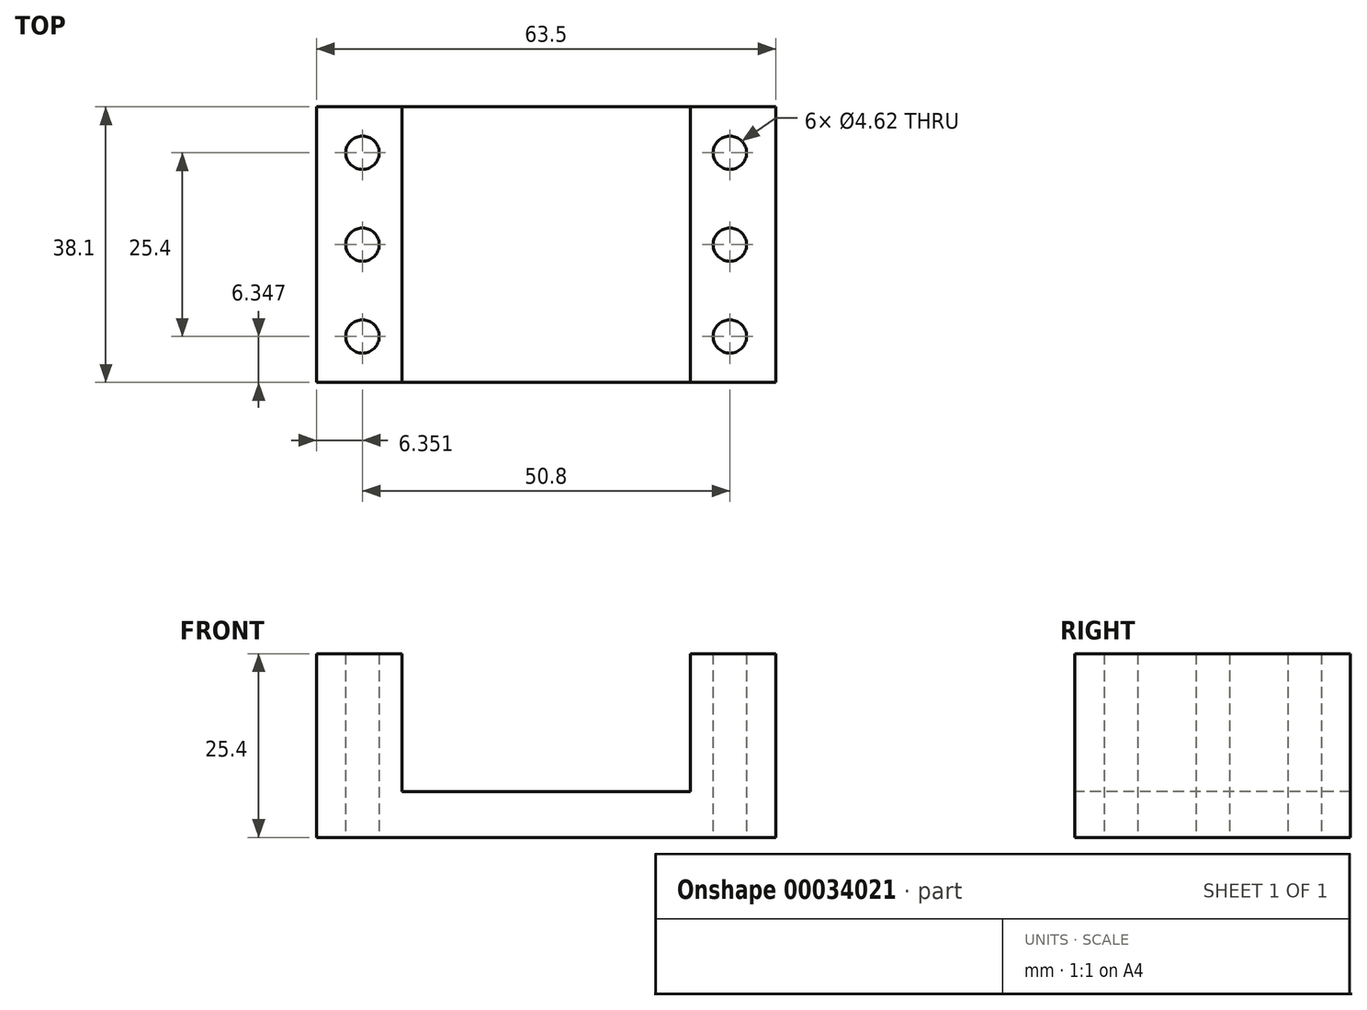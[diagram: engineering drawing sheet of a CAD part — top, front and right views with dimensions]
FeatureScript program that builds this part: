
annotation { "Feature Type Name" : "Feature", "Feature Type Description" : "" }
export const myFeature = defineFeature(function(context is Context, id is Id, definition is map)
    precondition{}
    {
        {
            var Q0;
            Q0=qCreatedBy(makeId("Top.planeOp"),FACE);
            var sketch = newSketch(context, id + "F0", { "sketchPlane" : qUnion([Q0])});
            skLineSegment(sketch, "E0.bottom", {"start": v(-27.54, 26.06) * mm, "end": v(35.96, 26.06) * mm});
            skLineSegment(sketch, "E0.top", {"start": v(-27.54, -12.04) * mm, "end": v(35.96, -12.04) * mm});
            skLineSegment(sketch, "E0.left", {"start": v(-27.54, 26.06) * mm, "end": v(-27.54, -12.04) * mm});
            skLineSegment(sketch, "E0.right", {"start": v(35.96, 26.06) * mm, "end": v(35.96, -12.04) * mm});
            skCircle(sketch, "E1", {"center": v(-21.19, 19.7) * mm, "radius": 2.31 * mm});
            skCircle(sketch, "E2.0.1.0", {"center": v(-21.19, 7) * mm, "radius": 2.31 * mm});
            skCircle(sketch, "E2.0.2.0", {"center": v(-21.19, -5.7) * mm, "radius": 2.31 * mm});
            skCircle(sketch, "E2.4.0.0", {"center": v(29.61, 19.7) * mm, "radius": 2.31 * mm});
            skCircle(sketch, "E2.4.1.0", {"center": v(29.61, 7) * mm, "radius": 2.31 * mm});
            skCircle(sketch, "E2.4.2.0", {"center": v(29.61, -5.7) * mm, "radius": 2.31 * mm});
            skLineSegment(sketch, "E3", {"start": v(-15.73, 26.06) * mm, "end": v(-15.73, -12.04) * mm});
            skPoint(sketch, "E3.startSnap0", {"position": v(-15.73, 19.7) * mm});
            skLineSegment(sketch, "E4", {"start": v(24.15, -12.04) * mm, "end": v(24.15, 26.06) * mm});
            skSolve(sketch);
        }
        {
            var Q0;
            {var subQ1=sQuery(id+"F0.wireOp",EDGE,"E0.left");Q0=makeQuery(id+"F0.imprint","IMPRINT",FACE,{"disambiguationData":[TD([[makeQuery(id+"F0.imprint","IMPRINT",EDGE,{"derivedFrom":subQ1}),1.0]])]});}
            var Q1;
            {var subQ1=sQuery(id+"F0.wireOp",EDGE,"E0.right");Q1=makeQuery(id+"F0.imprint","IMPRINT",FACE,{"disambiguationData":[TD([[makeQuery(id+"F0.imprint","IMPRINT",EDGE,{"derivedFrom":subQ1}),-1.0]])]});}
            extrude(context, id + "F1", {"entities" : qUnion([Q0, Q1]), "depth" : 25.4 * mm});
        }
        {
            var Q0;
            {var subQ1=sQuery(id+"F0.wireOp",EDGE,"E3");Q0=makeQuery(id+"F0.imprint","IMPRINT",FACE,{"disambiguationData":[TD([[makeQuery(id+"F0.imprint","IMPRINT",EDGE,{"derivedFrom":subQ1}),1.0]])]});}
            extrude(context, id + "F2", {"entities" : qUnion([Q0]), "operationType" : NewBodyOperationType.ADD, "depth" : 6.35 * mm});
        }
    });
